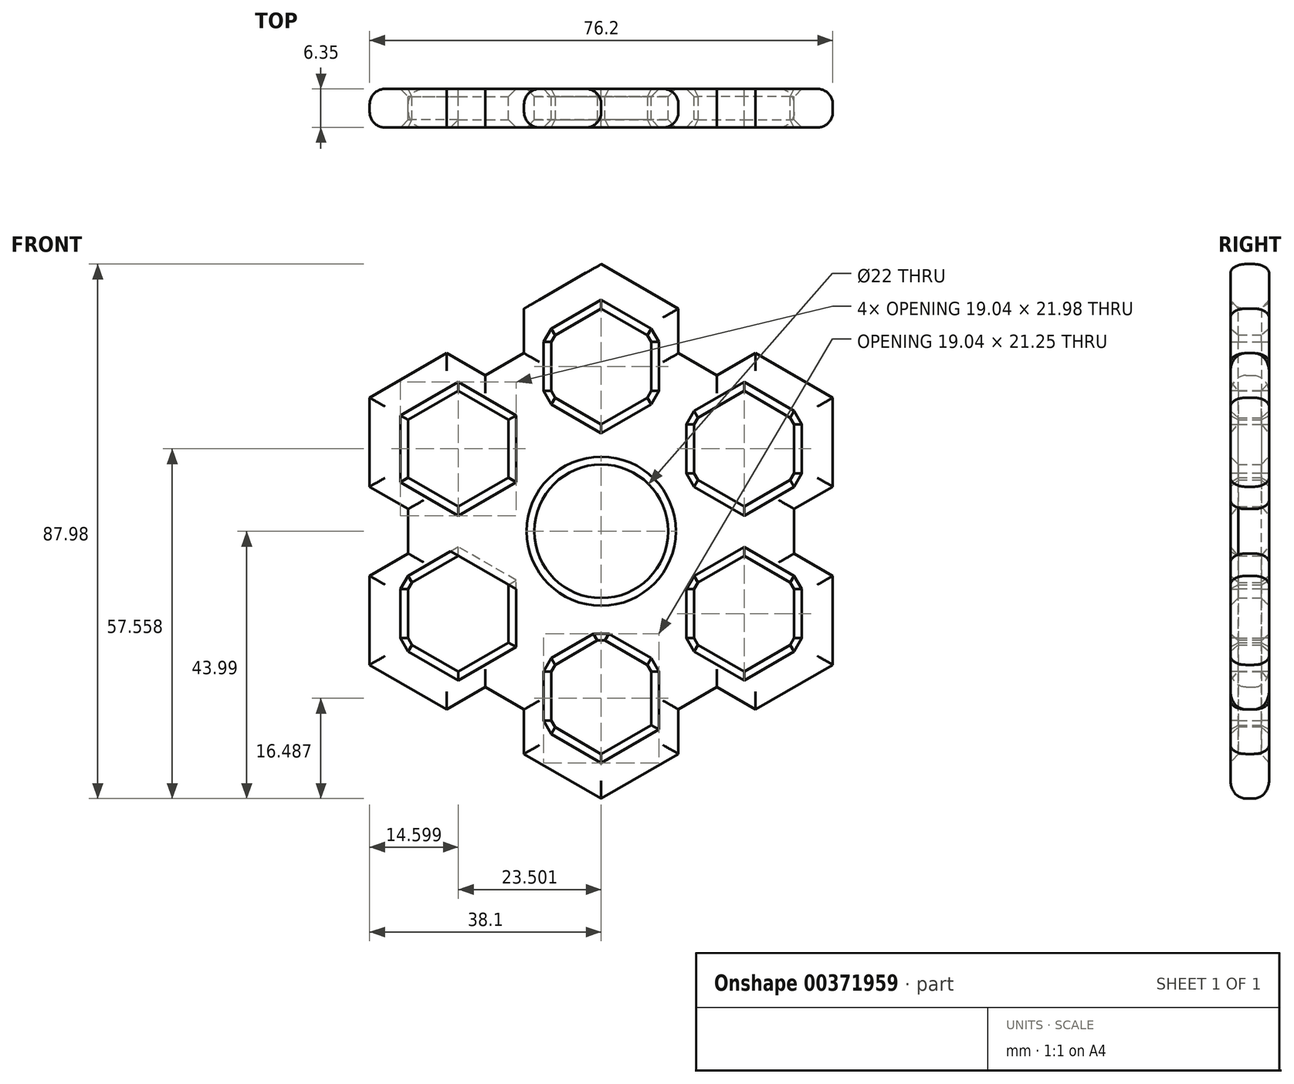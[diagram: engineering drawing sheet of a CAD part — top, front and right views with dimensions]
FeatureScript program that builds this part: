
annotation { "Feature Type Name" : "Feature", "Feature Type Description" : "" }
export const myFeature = defineFeature(function(context is Context, id is Id, definition is map)
    precondition{}
    {
        {
            var Q0;
            Q0=qCreatedBy(makeId("Front.planeOp"),FACE);
            var sketch = newSketch(context, id + "F0", { "sketchPlane" : qUnion([Q0])});
            skPoint(sketch, "E0", {"position": v(31.75, 0) * mm});
            skLineSegment(sketch, "E1.0", {"start": v(31.75, 18.33) * mm, "end": v(31.75, -18.33) * mm});
            skLineSegment(sketch, "E1.1", {"start": v(31.75, -18.33) * mm, "end": v(0, -36.66) * mm});
            skLineSegment(sketch, "E1.2", {"start": v(0, -36.66) * mm, "end": v(-31.75, -18.33) * mm});
            skLineSegment(sketch, "E1.3", {"start": v(-31.75, -18.33) * mm, "end": v(-31.75, 18.33) * mm});
            skLineSegment(sketch, "E1.4", {"start": v(-31.75, 18.33) * mm, "end": v(0, 36.66) * mm});
            skLineSegment(sketch, "E1.5", {"start": v(0, 36.66) * mm, "end": v(31.75, 18.33) * mm});
            skPoint(sketch, "E2.cCircle.center.orphan", {"position": v(0, 0) * mm});
            skCircle(sketch, "E3", {"center": v(0, 0) * mm, "radius": 11 * mm});
            skPoint(sketch, "E4", {"position": v(0, 27.14) * mm});
            skPoint(sketch, "E5", {"position": v(23.5, 13.57) * mm});
            skPoint(sketch, "E6", {"position": v(-23.5, 13.57) * mm});
            skPoint(sketch, "E7", {"position": v(-23.5, -13.57) * mm});
            skPoint(sketch, "E8", {"position": v(23.5, -13.57) * mm});
            skPoint(sketch, "E9", {"position": v(0, -27.14) * mm});
            skLineSegment(sketch, "E10.0", {"start": v(0, 36.66) * mm, "end": v(8.25, 31.9) * mm});
            skLineSegment(sketch, "E10.1", {"start": v(8.25, 31.9) * mm, "end": v(8.25, 22.37) * mm});
            skLineSegment(sketch, "E10.2", {"start": v(8.25, 22.37) * mm, "end": v(0, 17.61) * mm});
            skLineSegment(sketch, "E10.3", {"start": v(0, 17.61) * mm, "end": v(-8.25, 22.37) * mm});
            skLineSegment(sketch, "E10.4", {"start": v(-8.25, 22.37) * mm, "end": v(-8.25, 31.9) * mm});
            skLineSegment(sketch, "E10.5", {"start": v(-8.25, 31.9) * mm, "end": v(0, 36.66) * mm});
            skPoint(sketch, "E10.0.midPoint", {"position": v(4.12, 34.28) * mm});
            skLineSegment(sketch, "E11.0", {"start": v(8.25, -31.9) * mm, "end": v(0, -36.66) * mm});
            skLineSegment(sketch, "E11.1", {"start": v(0, -36.66) * mm, "end": v(-8.25, -31.9) * mm});
            skLineSegment(sketch, "E11.2", {"start": v(-8.25, -31.9) * mm, "end": v(-8.25, -22.37) * mm});
            skLineSegment(sketch, "E11.3", {"start": v(-8.25, -22.37) * mm, "end": v(0, -17.61) * mm});
            skLineSegment(sketch, "E11.4", {"start": v(0, -17.61) * mm, "end": v(8.25, -22.37) * mm});
            skLineSegment(sketch, "E11.5", {"start": v(8.25, -22.37) * mm, "end": v(8.25, -31.9) * mm});
            skPoint(sketch, "E11.0.midPoint", {"position": v(4.12, -34.28) * mm});
            skLineSegment(sketch, "E12.0", {"start": v(-31.75, 18.33) * mm, "end": v(-23.5, 23.1) * mm});
            skLineSegment(sketch, "E12.1", {"start": v(-23.5, 23.1) * mm, "end": v(-15.25, 18.33) * mm});
            skLineSegment(sketch, "E12.2", {"start": v(-15.25, 18.33) * mm, "end": v(-15.25, 8.8) * mm});
            skLineSegment(sketch, "E12.3", {"start": v(-15.25, 8.8) * mm, "end": v(-23.5, 4.04) * mm});
            skLineSegment(sketch, "E12.4", {"start": v(-23.5, 4.04) * mm, "end": v(-31.75, 8.8) * mm});
            skLineSegment(sketch, "E12.5", {"start": v(-31.75, 8.8) * mm, "end": v(-31.75, 18.33) * mm});
            skPoint(sketch, "E12.0.midPoint", {"position": v(-27.63, 20.71) * mm});
            skLineSegment(sketch, "E13.0", {"start": v(-31.75, -18.33) * mm, "end": v(-31.75, -8.8) * mm});
            skLineSegment(sketch, "E13.1", {"start": v(-31.75, -8.8) * mm, "end": v(-23.5, -4.04) * mm});
            skLineSegment(sketch, "E13.2", {"start": v(-23.5, -4.04) * mm, "end": v(-15.25, -8.8) * mm});
            skLineSegment(sketch, "E13.3", {"start": v(-15.25, -8.8) * mm, "end": v(-15.25, -18.33) * mm});
            skLineSegment(sketch, "E13.4", {"start": v(-15.25, -18.33) * mm, "end": v(-23.5, -23.1) * mm});
            skLineSegment(sketch, "E13.5", {"start": v(-23.5, -23.1) * mm, "end": v(-31.75, -18.33) * mm});
            skPoint(sketch, "E13.0.midPoint", {"position": v(-31.75, -13.57) * mm});
            skLineSegment(sketch, "E14.0", {"start": v(31.75, -18.33) * mm, "end": v(23.5, -23.1) * mm});
            skLineSegment(sketch, "E14.1", {"start": v(23.5, -23.1) * mm, "end": v(15.25, -18.33) * mm});
            skLineSegment(sketch, "E14.2", {"start": v(15.25, -18.33) * mm, "end": v(15.25, -8.8) * mm});
            skLineSegment(sketch, "E14.3", {"start": v(15.25, -8.8) * mm, "end": v(23.5, -4.04) * mm});
            skLineSegment(sketch, "E14.4", {"start": v(23.5, -4.04) * mm, "end": v(31.75, -8.8) * mm});
            skLineSegment(sketch, "E14.5", {"start": v(31.75, -8.8) * mm, "end": v(31.75, -18.33) * mm});
            skPoint(sketch, "E14.0.midPoint", {"position": v(27.63, -20.71) * mm});
            skLineSegment(sketch, "E15.0", {"start": v(31.75, 18.33) * mm, "end": v(31.75, 8.8) * mm});
            skLineSegment(sketch, "E15.1", {"start": v(31.75, 8.8) * mm, "end": v(23.5, 4.04) * mm});
            skLineSegment(sketch, "E15.2", {"start": v(23.5, 4.04) * mm, "end": v(15.25, 8.8) * mm});
            skLineSegment(sketch, "E15.3", {"start": v(15.25, 8.8) * mm, "end": v(15.25, 18.33) * mm});
            skLineSegment(sketch, "E15.4", {"start": v(15.25, 18.33) * mm, "end": v(23.5, 23.1) * mm});
            skLineSegment(sketch, "E15.5", {"start": v(23.5, 23.1) * mm, "end": v(31.75, 18.33) * mm});
            skPoint(sketch, "E15.0.midPoint", {"position": v(31.75, 13.57) * mm});
            skArc(sketch, "E16.trimOffspring", {"start": v(-4.12, 34.28) * mm, "mid": v(-7.14, 31.26) * mm, "end": v(-8.25, 27.14) * mm, "construction": true});
            skPoint(sketch, "E17", {"position": v(38.1, 0) * mm});
            skLineSegment(sketch, "E18.0", {"start": v(38.1, 22) * mm, "end": v(38.1, -22) * mm});
            skLineSegment(sketch, "E18.1", {"start": v(38.1, -22) * mm, "end": v(0, -44) * mm});
            skLineSegment(sketch, "E18.2", {"start": v(0, -44) * mm, "end": v(-38.1, -22) * mm});
            skLineSegment(sketch, "E18.3", {"start": v(-38.1, -22) * mm, "end": v(-38.1, 22) * mm});
            skLineSegment(sketch, "E18.4", {"start": v(-38.1, 22) * mm, "end": v(-25.4, 29.33) * mm});
            skLineSegment(sketch, "E18.5", {"start": v(0, 44) * mm, "end": v(38.1, 22) * mm});
            skLineSegment(sketch, "E19.0", {"start": v(-12.7, 29.33) * mm, "end": v(-19.05, 25.66) * mm});
            skLineSegment(sketch, "E19.1", {"start": v(-19.05, 25.66) * mm, "end": v(-25.4, 29.33) * mm});
            skLineSegment(sketch, "E19.5", {"start": v(-12.7, 36.66) * mm, "end": v(-12.7, 29.33) * mm});
            skPoint(sketch, "E19.0.midPoint", {"position": v(-15.88, 27.5) * mm});
            skCircle(sketch, "E20.cCircle", {"center": v(19.05, 33) * mm, "radius": 6.35 * mm, "construction": true});
            skLineSegment(sketch, "E20.0", {"start": v(19.05, 25.66) * mm, "end": v(12.7, 29.33) * mm});
            skLineSegment(sketch, "E20.1", {"start": v(12.7, 29.33) * mm, "end": v(12.7, 36.66) * mm});
            skLineSegment(sketch, "E20.2", {"start": v(12.7, 36.66) * mm, "end": v(19.05, 40.33) * mm});
            skLineSegment(sketch, "E20.3", {"start": v(19.05, 40.33) * mm, "end": v(25.4, 36.66) * mm});
            skLineSegment(sketch, "E20.4", {"start": v(25.4, 36.66) * mm, "end": v(25.4, 29.33) * mm});
            skLineSegment(sketch, "E20.5", {"start": v(25.4, 29.33) * mm, "end": v(19.05, 25.66) * mm});
            skPoint(sketch, "E20.0.midPoint", {"position": v(15.87, 27.5) * mm});
            skCircle(sketch, "E21.cCircle", {"center": v(38.1, 0) * mm, "radius": 6.35 * mm, "construction": true});
            skLineSegment(sketch, "E21.0", {"start": v(31.75, -3.67) * mm, "end": v(31.75, 3.67) * mm});
            skLineSegment(sketch, "E21.1", {"start": v(31.75, 3.67) * mm, "end": v(38.1, 7.33) * mm});
            skLineSegment(sketch, "E21.2", {"start": v(38.1, 7.33) * mm, "end": v(44.45, 3.67) * mm});
            skLineSegment(sketch, "E21.3", {"start": v(44.45, 3.67) * mm, "end": v(44.45, -3.67) * mm});
            skLineSegment(sketch, "E21.4", {"start": v(44.45, -3.67) * mm, "end": v(38.1, -7.33) * mm});
            skLineSegment(sketch, "E21.5", {"start": v(38.1, -7.33) * mm, "end": v(31.75, -3.67) * mm});
            skCircle(sketch, "E22.cCircle", {"center": v(19.05, -33) * mm, "radius": 6.35 * mm, "construction": true});
            skLineSegment(sketch, "E22.0", {"start": v(12.7, -29.33) * mm, "end": v(19.05, -25.66) * mm});
            skLineSegment(sketch, "E22.1", {"start": v(19.05, -25.66) * mm, "end": v(25.4, -29.33) * mm});
            skLineSegment(sketch, "E22.2", {"start": v(25.4, -29.33) * mm, "end": v(25.4, -36.66) * mm});
            skLineSegment(sketch, "E22.3", {"start": v(25.4, -36.66) * mm, "end": v(19.05, -40.33) * mm});
            skLineSegment(sketch, "E22.4", {"start": v(19.05, -40.33) * mm, "end": v(12.7, -36.66) * mm});
            skLineSegment(sketch, "E22.5", {"start": v(12.7, -36.66) * mm, "end": v(12.7, -29.33) * mm});
            skPoint(sketch, "E22.0.midPoint", {"position": v(15.87, -27.5) * mm});
            skCircle(sketch, "E23.cCircle", {"center": v(-19.05, -33) * mm, "radius": 6.35 * mm, "construction": true});
            skLineSegment(sketch, "E23.0", {"start": v(-19.05, -25.66) * mm, "end": v(-12.7, -29.33) * mm});
            skLineSegment(sketch, "E23.1", {"start": v(-12.7, -29.33) * mm, "end": v(-12.7, -36.66) * mm});
            skLineSegment(sketch, "E23.2", {"start": v(-12.7, -36.66) * mm, "end": v(-19.05, -40.33) * mm});
            skLineSegment(sketch, "E23.3", {"start": v(-19.05, -40.33) * mm, "end": v(-25.4, -36.66) * mm});
            skLineSegment(sketch, "E23.4", {"start": v(-25.4, -36.66) * mm, "end": v(-25.4, -29.33) * mm});
            skLineSegment(sketch, "E23.5", {"start": v(-25.4, -29.33) * mm, "end": v(-19.05, -25.66) * mm});
            skPoint(sketch, "E23.0.midPoint", {"position": v(-15.88, -27.5) * mm});
            skCircle(sketch, "E24.cCircle", {"center": v(-38.1, 0) * mm, "radius": 6.35 * mm, "construction": true});
            skLineSegment(sketch, "E24.0", {"start": v(-31.75, 3.67) * mm, "end": v(-31.75, -3.67) * mm});
            skLineSegment(sketch, "E24.1", {"start": v(-31.75, -3.67) * mm, "end": v(-38.1, -7.33) * mm});
            skLineSegment(sketch, "E24.2", {"start": v(-38.1, -7.33) * mm, "end": v(-44.45, -3.67) * mm});
            skLineSegment(sketch, "E24.3", {"start": v(-44.45, -3.67) * mm, "end": v(-44.45, 3.67) * mm});
            skLineSegment(sketch, "E24.4", {"start": v(-44.45, 3.67) * mm, "end": v(-38.1, 7.33) * mm});
            skLineSegment(sketch, "E24.5", {"start": v(-38.1, 7.33) * mm, "end": v(-31.75, 3.67) * mm});
            skPoint(sketch, "E24.0.midPoint", {"position": v(-31.75, 0) * mm});
            skLineSegment(sketch, "E25.trimOffspring", {"start": v(-12.7, 36.66) * mm, "end": v(0, 44) * mm});
            skSolve(sketch);
        }
        {
            var Q0;
            Q0=makeQuery(id+"F0.imprint","IMPRINT",FACE,{"disambiguationData":[TD([[makeQuery(id+"F0.imprint","IMPRINT",EDGE,{"derivedFrom":sQuery(id+"F0.wireOp",EDGE,"E3")}),-1.0]])]});
            var Q1;
            {var subQ2=sQuery(id+"F0.wireOp",EDGE,"E20.5");Q1=makeQuery(id+"F0.imprint","IMPRINT",FACE,{"disambiguationData":[TD([[makeQuery(id+"F0.imprint","IMPRINT",EDGE,{"derivedFrom":subQ2}),1.0]])]});}
            var Q2;
            {var subQ6=sQuery(id+"F0.wireOp",EDGE,"E21.5");Q2=makeQuery(id+"F0.imprint","IMPRINT",FACE,{"disambiguationData":[TD([[makeQuery(id+"F0.imprint","IMPRINT",EDGE,{"derivedFrom":subQ6}),1.0]])]});}
            var Q3;
            {var subQ5=sQuery(id+"F0.wireOp",EDGE,"E22.5");Q3=makeQuery(id+"F0.imprint","IMPRINT",FACE,{"disambiguationData":[TD([[makeQuery(id+"F0.imprint","IMPRINT",EDGE,{"derivedFrom":subQ5}),1.0]])]});}
            var Q4;
            {var subQ3=sQuery(id+"F0.wireOp",EDGE,"E23.5");Q4=makeQuery(id+"F0.imprint","IMPRINT",FACE,{"disambiguationData":[TD([[makeQuery(id+"F0.imprint","IMPRINT",EDGE,{"derivedFrom":subQ3}),1.0]])]});}
            var Q5;
            {var subQ0=sQuery(id+"F0.wireOp",EDGE,"E19.1");Q5=makeQuery(id+"F0.imprint","IMPRINT",FACE,{"disambiguationData":[TD([[makeQuery(id+"F0.imprint","IMPRINT",EDGE,{"derivedFrom":subQ0}),1.0]])]});}
            var Q6;
            {var subQ6=sQuery(id+"F0.wireOp",EDGE,"E19.5");Q6=makeQuery(id+"F0.imprint","IMPRINT",FACE,{"disambiguationData":[TD([[makeQuery(id+"F0.imprint","IMPRINT",EDGE,{"derivedFrom":subQ6}),1.0]])]});}
            extrude(context, id + "F1", {"entities" : qUnion([Q0, Q1, Q2, Q3, Q4, Q5, Q6]), "depth" : 6.35 * mm, "offsetDistance" : 25.4 * mm});
        }
        {
            var Q0;
            Q0=makeQuery(id+"F1.opExtrude","CAP_EDGE",EDGE,{"disambiguationData":[OSD([sQuery(id+"F0.wireOp",EDGE,"E19.1")])],"isStart":false});
            var Q1;
            {var subQ0=sQuery(id+"F0.wireOp",EDGE,"E1.4");Q1=makeQuery(id+"F1.opExtrude","CAP_EDGE",EDGE,{"disambiguationData":[OSD([subQ0]),TDD([makeQuery(id+"F0.imprint","IMPRINT",EDGE,{"disambiguationData":[TD([[makeQuery(id+"F0.imprint","INTERSECT",VERTEX,{"derivedFrom":[subQ0,sQuery(id+"F0.wireOp",EDGE,"E19.1")]}),-1.0]])],"derivedFrom":subQ0})])],"isStart":false});}
            var Q2;
            Q2=makeQuery(id+"F1.opExtrude","CAP_EDGE",EDGE,{"disambiguationData":[OSD([sQuery(id+"F0.wireOp",EDGE,"E19.5")])],"isStart":false});
            var Q3;
            {var subQ0=sQuery(id+"F0.wireOp",EDGE,"E18.4");Q3=makeQuery(id+"F1.opExtrude","CAP_EDGE",EDGE,{"disambiguationData":[OSD([subQ0]),TDD([makeQuery(id+"F0.imprint","IMPRINT",EDGE,{"disambiguationData":[TD([[makeQuery(id+"F0.imprint","INTERSECT",VERTEX,{"derivedFrom":[subQ0,sQuery(id+"F0.wireOp",EDGE,"E18.5")]}),1.0]])],"derivedFrom":subQ0})])],"isStart":false});}
            var Q4;
            {var subQ0=sQuery(id+"F0.wireOp",EDGE,"E18.5");Q4=makeQuery(id+"F1.opExtrude","CAP_EDGE",EDGE,{"disambiguationData":[OSD([subQ0]),TDD([makeQuery(id+"F0.imprint","IMPRINT",EDGE,{"disambiguationData":[TD([[makeQuery(id+"F0.imprint","INTERSECT",VERTEX,{"derivedFrom":[sQuery(id+"F0.wireOp",EDGE,"E18.4"),subQ0]}),-1.0]])],"derivedFrom":subQ0})])],"isStart":false});}
            var Q5;
            Q5=makeQuery(id+"F1.opExtrude","CAP_EDGE",EDGE,{"disambiguationData":[OSD([sQuery(id+"F0.wireOp",EDGE,"E20.1")])],"isStart":false});
            var Q6;
            {var subQ0=sQuery(id+"F0.wireOp",EDGE,"E1.5");Q6=makeQuery(id+"F1.opExtrude","CAP_EDGE",EDGE,{"disambiguationData":[OSD([subQ0]),TDD([makeQuery(id+"F0.imprint","IMPRINT",EDGE,{"disambiguationData":[TD([[makeQuery(id+"F0.imprint","INTERSECT",VERTEX,{"derivedFrom":[subQ0,sQuery(id+"F0.wireOp",EDGE,"E20.1")]}),-1.0]])],"derivedFrom":subQ0})])],"isStart":false});}
            var Q7;
            Q7=makeQuery(id+"F1.opExtrude","CAP_EDGE",EDGE,{"disambiguationData":[OSD([sQuery(id+"F0.wireOp",EDGE,"E20.5")])],"isStart":false});
            var Q8;
            {var subQ0=sQuery(id+"F0.wireOp",EDGE,"E18.5");Q8=makeQuery(id+"F1.opExtrude","CAP_EDGE",EDGE,{"disambiguationData":[OSD([subQ0]),TDD([makeQuery(id+"F0.imprint","IMPRINT",EDGE,{"disambiguationData":[TD([[makeQuery(id+"F0.imprint","INTERSECT",VERTEX,{"derivedFrom":[sQuery(id+"F0.wireOp",EDGE,"E18.0"),subQ0]}),1.0]])],"derivedFrom":subQ0})])],"isStart":false});}
            var Q9;
            {var subQ0=sQuery(id+"F0.wireOp",EDGE,"E18.0");Q9=makeQuery(id+"F1.opExtrude","CAP_EDGE",EDGE,{"disambiguationData":[OSD([subQ0]),TDD([makeQuery(id+"F0.imprint","IMPRINT",EDGE,{"disambiguationData":[TD([[makeQuery(id+"F0.imprint","INTERSECT",VERTEX,{"derivedFrom":[subQ0,sQuery(id+"F0.wireOp",EDGE,"E18.5")]}),-1.0]])],"derivedFrom":subQ0})])],"isStart":false});}
            var Q10;
            Q10=makeQuery(id+"F1.opExtrude","CAP_EDGE",EDGE,{"disambiguationData":[OSD([sQuery(id+"F0.wireOp",EDGE,"E21.1")])],"isStart":false});
            var Q11;
            {var subQ0=sQuery(id+"F0.wireOp",EDGE,"E1.0");Q11=makeQuery(id+"F1.opExtrude","CAP_EDGE",EDGE,{"disambiguationData":[OSD([subQ0]),TDD([makeQuery(id+"F0.imprint","IMPRINT",EDGE,{"disambiguationData":[TD([[makeQuery(id+"F0.imprint","INTERSECT",VERTEX,{"derivedFrom":[subQ0,sQuery(id+"F0.wireOp",EDGE,"E21.1")]}),-1.0]])],"derivedFrom":subQ0})])],"isStart":false});}
            var Q12;
            Q12=makeQuery(id+"F1.opExtrude","CAP_EDGE",EDGE,{"disambiguationData":[OSD([sQuery(id+"F0.wireOp",EDGE,"E21.5")])],"isStart":false});
            var Q13;
            {var subQ0=sQuery(id+"F0.wireOp",EDGE,"E18.0");Q13=makeQuery(id+"F1.opExtrude","CAP_EDGE",EDGE,{"disambiguationData":[OSD([subQ0]),TDD([makeQuery(id+"F0.imprint","IMPRINT",EDGE,{"disambiguationData":[TD([[makeQuery(id+"F0.imprint","INTERSECT",VERTEX,{"derivedFrom":[subQ0,sQuery(id+"F0.wireOp",EDGE,"E18.1")]}),1.0]])],"derivedFrom":subQ0})])],"isStart":false});}
            var Q14;
            {var subQ0=sQuery(id+"F0.wireOp",EDGE,"E18.1");Q14=makeQuery(id+"F1.opExtrude","CAP_EDGE",EDGE,{"disambiguationData":[OSD([subQ0]),TDD([makeQuery(id+"F0.imprint","IMPRINT",EDGE,{"disambiguationData":[TD([[makeQuery(id+"F0.imprint","INTERSECT",VERTEX,{"derivedFrom":[sQuery(id+"F0.wireOp",EDGE,"E18.0"),subQ0]}),-1.0]])],"derivedFrom":subQ0})])],"isStart":false});}
            var Q15;
            Q15=makeQuery(id+"F1.opExtrude","CAP_EDGE",EDGE,{"disambiguationData":[OSD([sQuery(id+"F0.wireOp",EDGE,"E22.1")])],"isStart":false});
            var Q16;
            {var subQ0=sQuery(id+"F0.wireOp",EDGE,"E1.1");Q16=makeQuery(id+"F1.opExtrude","CAP_EDGE",EDGE,{"disambiguationData":[OSD([subQ0]),TDD([makeQuery(id+"F0.imprint","IMPRINT",EDGE,{"disambiguationData":[TD([[makeQuery(id+"F0.imprint","INTERSECT",VERTEX,{"derivedFrom":[subQ0,sQuery(id+"F0.wireOp",EDGE,"E22.1")]}),-1.0]])],"derivedFrom":subQ0})])],"isStart":false});}
            var Q17;
            Q17=makeQuery(id+"F1.opExtrude","CAP_EDGE",EDGE,{"disambiguationData":[OSD([sQuery(id+"F0.wireOp",EDGE,"E22.5")])],"isStart":false});
            var Q18;
            {var subQ0=sQuery(id+"F0.wireOp",EDGE,"E18.1");Q18=makeQuery(id+"F1.opExtrude","CAP_EDGE",EDGE,{"disambiguationData":[OSD([subQ0]),TDD([makeQuery(id+"F0.imprint","IMPRINT",EDGE,{"disambiguationData":[TD([[makeQuery(id+"F0.imprint","INTERSECT",VERTEX,{"derivedFrom":[subQ0,sQuery(id+"F0.wireOp",EDGE,"E18.2")]}),1.0]])],"derivedFrom":subQ0})])],"isStart":false});}
            var Q19;
            {var subQ0=sQuery(id+"F0.wireOp",EDGE,"E18.2");Q19=makeQuery(id+"F1.opExtrude","CAP_EDGE",EDGE,{"disambiguationData":[OSD([subQ0]),TDD([makeQuery(id+"F0.imprint","IMPRINT",EDGE,{"disambiguationData":[TD([[makeQuery(id+"F0.imprint","INTERSECT",VERTEX,{"derivedFrom":[sQuery(id+"F0.wireOp",EDGE,"E18.1"),subQ0]}),-1.0]])],"derivedFrom":subQ0})])],"isStart":false});}
            var Q20;
            Q20=makeQuery(id+"F1.opExtrude","CAP_EDGE",EDGE,{"disambiguationData":[OSD([sQuery(id+"F0.wireOp",EDGE,"E23.1")])],"isStart":false});
            var Q21;
            {var subQ0=sQuery(id+"F0.wireOp",EDGE,"E1.2");Q21=makeQuery(id+"F1.opExtrude","CAP_EDGE",EDGE,{"disambiguationData":[OSD([subQ0]),TDD([makeQuery(id+"F0.imprint","IMPRINT",EDGE,{"disambiguationData":[TD([[makeQuery(id+"F0.imprint","INTERSECT",VERTEX,{"derivedFrom":[subQ0,sQuery(id+"F0.wireOp",EDGE,"E23.1")]}),-1.0]])],"derivedFrom":subQ0})])],"isStart":false});}
            var Q22;
            Q22=makeQuery(id+"F1.opExtrude","CAP_EDGE",EDGE,{"disambiguationData":[OSD([sQuery(id+"F0.wireOp",EDGE,"E23.5")])],"isStart":false});
            var Q23;
            {var subQ0=sQuery(id+"F0.wireOp",EDGE,"E18.2");Q23=makeQuery(id+"F1.opExtrude","CAP_EDGE",EDGE,{"disambiguationData":[OSD([subQ0]),TDD([makeQuery(id+"F0.imprint","IMPRINT",EDGE,{"disambiguationData":[TD([[makeQuery(id+"F0.imprint","INTERSECT",VERTEX,{"derivedFrom":[subQ0,sQuery(id+"F0.wireOp",EDGE,"E18.3")]}),1.0]])],"derivedFrom":subQ0})])],"isStart":false});}
            var Q24;
            {var subQ0=sQuery(id+"F0.wireOp",EDGE,"E18.3");Q24=makeQuery(id+"F1.opExtrude","CAP_EDGE",EDGE,{"disambiguationData":[OSD([subQ0]),TDD([makeQuery(id+"F0.imprint","IMPRINT",EDGE,{"disambiguationData":[TD([[makeQuery(id+"F0.imprint","INTERSECT",VERTEX,{"derivedFrom":[sQuery(id+"F0.wireOp",EDGE,"E18.2"),subQ0]}),-1.0]])],"derivedFrom":subQ0})])],"isStart":false});}
            var Q25;
            Q25=makeQuery(id+"F1.opExtrude","CAP_EDGE",EDGE,{"disambiguationData":[OSD([sQuery(id+"F0.wireOp",EDGE,"E24.1")])],"isStart":false});
            var Q26;
            {var subQ0=sQuery(id+"F0.wireOp",EDGE,"E18.4");Q26=makeQuery(id+"F1.opExtrude","CAP_EDGE",EDGE,{"disambiguationData":[OSD([subQ0]),TDD([makeQuery(id+"F0.imprint","IMPRINT",EDGE,{"disambiguationData":[TD([[makeQuery(id+"F0.imprint","INTERSECT",VERTEX,{"derivedFrom":[sQuery(id+"F0.wireOp",EDGE,"E18.3"),subQ0]}),-1.0]])],"derivedFrom":subQ0})])],"isStart":false});}
            var Q27;
            {var subQ0=sQuery(id+"F0.wireOp",EDGE,"E1.3");Q27=makeQuery(id+"F1.opExtrude","CAP_EDGE",EDGE,{"disambiguationData":[OSD([subQ0]),TDD([makeQuery(id+"F0.imprint","IMPRINT",EDGE,{"disambiguationData":[TD([[makeQuery(id+"F0.imprint","INTERSECT",VERTEX,{"derivedFrom":[subQ0,sQuery(id+"F0.wireOp",EDGE,"E24.1")]}),-1.0]])],"derivedFrom":subQ0})])],"isStart":false});}
            var Q28;
            Q28=makeQuery(id+"F1.opExtrude","CAP_EDGE",EDGE,{"disambiguationData":[OSD([sQuery(id+"F0.wireOp",EDGE,"E24.5")])],"isStart":false});
            var Q29;
            {var subQ0=sQuery(id+"F0.wireOp",EDGE,"E18.3");Q29=makeQuery(id+"F1.opExtrude","CAP_EDGE",EDGE,{"disambiguationData":[OSD([subQ0]),TDD([makeQuery(id+"F0.imprint","IMPRINT",EDGE,{"disambiguationData":[TD([[makeQuery(id+"F0.imprint","INTERSECT",VERTEX,{"derivedFrom":[subQ0,sQuery(id+"F0.wireOp",EDGE,"E18.4")]}),1.0]])],"derivedFrom":subQ0})])],"isStart":false});}
            var Q30;
            {var subQ0=sQuery(id+"F0.wireOp",EDGE,"E18.4");Q30=makeQuery(id+"F1.opExtrude","CAP_EDGE",EDGE,{"disambiguationData":[OSD([subQ0]),TDD([makeQuery(id+"F0.imprint","IMPRINT",EDGE,{"disambiguationData":[TD([[makeQuery(id+"F0.imprint","INTERSECT",VERTEX,{"derivedFrom":[subQ0,sQuery(id+"F0.wireOp",EDGE,"E18.5")]}),1.0]])],"derivedFrom":subQ0})])],"isStart":true});}
            var Q31;
            {var subQ0=sQuery(id+"F0.wireOp",EDGE,"E18.5");Q31=makeQuery(id+"F1.opExtrude","CAP_EDGE",EDGE,{"disambiguationData":[OSD([subQ0]),TDD([makeQuery(id+"F0.imprint","IMPRINT",EDGE,{"disambiguationData":[TD([[makeQuery(id+"F0.imprint","INTERSECT",VERTEX,{"derivedFrom":[sQuery(id+"F0.wireOp",EDGE,"E18.4"),subQ0]}),-1.0]])],"derivedFrom":subQ0})])],"isStart":true});}
            var Q32;
            Q32=makeQuery(id+"F1.opExtrude","CAP_EDGE",EDGE,{"disambiguationData":[OSD([sQuery(id+"F0.wireOp",EDGE,"E20.1")])],"isStart":true});
            var Q33;
            {var subQ0=sQuery(id+"F0.wireOp",EDGE,"E1.5");Q33=makeQuery(id+"F1.opExtrude","CAP_EDGE",EDGE,{"disambiguationData":[OSD([subQ0]),TDD([makeQuery(id+"F0.imprint","IMPRINT",EDGE,{"disambiguationData":[TD([[makeQuery(id+"F0.imprint","INTERSECT",VERTEX,{"derivedFrom":[subQ0,sQuery(id+"F0.wireOp",EDGE,"E20.1")]}),-1.0]])],"derivedFrom":subQ0})])],"isStart":true});}
            var Q34;
            Q34=makeQuery(id+"F1.opExtrude","CAP_EDGE",EDGE,{"disambiguationData":[OSD([sQuery(id+"F0.wireOp",EDGE,"E20.5")])],"isStart":true});
            var Q35;
            {var subQ0=sQuery(id+"F0.wireOp",EDGE,"E18.5");Q35=makeQuery(id+"F1.opExtrude","CAP_EDGE",EDGE,{"disambiguationData":[OSD([subQ0]),TDD([makeQuery(id+"F0.imprint","IMPRINT",EDGE,{"disambiguationData":[TD([[makeQuery(id+"F0.imprint","INTERSECT",VERTEX,{"derivedFrom":[sQuery(id+"F0.wireOp",EDGE,"E18.0"),subQ0]}),1.0]])],"derivedFrom":subQ0})])],"isStart":true});}
            var Q36;
            {var subQ0=sQuery(id+"F0.wireOp",EDGE,"E18.0");Q36=makeQuery(id+"F1.opExtrude","CAP_EDGE",EDGE,{"disambiguationData":[OSD([subQ0]),TDD([makeQuery(id+"F0.imprint","IMPRINT",EDGE,{"disambiguationData":[TD([[makeQuery(id+"F0.imprint","INTERSECT",VERTEX,{"derivedFrom":[subQ0,sQuery(id+"F0.wireOp",EDGE,"E18.5")]}),-1.0]])],"derivedFrom":subQ0})])],"isStart":true});}
            var Q37;
            Q37=makeQuery(id+"F1.opExtrude","CAP_EDGE",EDGE,{"disambiguationData":[OSD([sQuery(id+"F0.wireOp",EDGE,"E21.1")])],"isStart":true});
            var Q38;
            {var subQ0=sQuery(id+"F0.wireOp",EDGE,"E1.0");Q38=makeQuery(id+"F1.opExtrude","CAP_EDGE",EDGE,{"disambiguationData":[OSD([subQ0]),TDD([makeQuery(id+"F0.imprint","IMPRINT",EDGE,{"disambiguationData":[TD([[makeQuery(id+"F0.imprint","INTERSECT",VERTEX,{"derivedFrom":[subQ0,sQuery(id+"F0.wireOp",EDGE,"E21.1")]}),-1.0]])],"derivedFrom":subQ0})])],"isStart":true});}
            var Q39;
            Q39=makeQuery(id+"F1.opExtrude","CAP_EDGE",EDGE,{"disambiguationData":[OSD([sQuery(id+"F0.wireOp",EDGE,"E21.5")])],"isStart":true});
            var Q40;
            {var subQ0=sQuery(id+"F0.wireOp",EDGE,"E18.0");Q40=makeQuery(id+"F1.opExtrude","CAP_EDGE",EDGE,{"disambiguationData":[OSD([subQ0]),TDD([makeQuery(id+"F0.imprint","IMPRINT",EDGE,{"disambiguationData":[TD([[makeQuery(id+"F0.imprint","INTERSECT",VERTEX,{"derivedFrom":[subQ0,sQuery(id+"F0.wireOp",EDGE,"E18.1")]}),1.0]])],"derivedFrom":subQ0})])],"isStart":true});}
            var Q41;
            {var subQ0=sQuery(id+"F0.wireOp",EDGE,"E18.1");Q41=makeQuery(id+"F1.opExtrude","CAP_EDGE",EDGE,{"disambiguationData":[OSD([subQ0]),TDD([makeQuery(id+"F0.imprint","IMPRINT",EDGE,{"disambiguationData":[TD([[makeQuery(id+"F0.imprint","INTERSECT",VERTEX,{"derivedFrom":[sQuery(id+"F0.wireOp",EDGE,"E18.0"),subQ0]}),-1.0]])],"derivedFrom":subQ0})])],"isStart":true});}
            var Q42;
            Q42=makeQuery(id+"F1.opExtrude","CAP_EDGE",EDGE,{"disambiguationData":[OSD([sQuery(id+"F0.wireOp",EDGE,"E22.1")])],"isStart":true});
            var Q43;
            {var subQ0=sQuery(id+"F0.wireOp",EDGE,"E1.1");Q43=makeQuery(id+"F1.opExtrude","CAP_EDGE",EDGE,{"disambiguationData":[OSD([subQ0]),TDD([makeQuery(id+"F0.imprint","IMPRINT",EDGE,{"disambiguationData":[TD([[makeQuery(id+"F0.imprint","INTERSECT",VERTEX,{"derivedFrom":[subQ0,sQuery(id+"F0.wireOp",EDGE,"E22.1")]}),-1.0]])],"derivedFrom":subQ0})])],"isStart":true});}
            var Q44;
            Q44=makeQuery(id+"F1.opExtrude","CAP_EDGE",EDGE,{"disambiguationData":[OSD([sQuery(id+"F0.wireOp",EDGE,"E22.5")])],"isStart":true});
            var Q45;
            {var subQ0=sQuery(id+"F0.wireOp",EDGE,"E18.1");Q45=makeQuery(id+"F1.opExtrude","CAP_EDGE",EDGE,{"disambiguationData":[OSD([subQ0]),TDD([makeQuery(id+"F0.imprint","IMPRINT",EDGE,{"disambiguationData":[TD([[makeQuery(id+"F0.imprint","INTERSECT",VERTEX,{"derivedFrom":[subQ0,sQuery(id+"F0.wireOp",EDGE,"E18.2")]}),1.0]])],"derivedFrom":subQ0})])],"isStart":true});}
            var Q46;
            {var subQ0=sQuery(id+"F0.wireOp",EDGE,"E18.2");Q46=makeQuery(id+"F1.opExtrude","CAP_EDGE",EDGE,{"disambiguationData":[OSD([subQ0]),TDD([makeQuery(id+"F0.imprint","IMPRINT",EDGE,{"disambiguationData":[TD([[makeQuery(id+"F0.imprint","INTERSECT",VERTEX,{"derivedFrom":[sQuery(id+"F0.wireOp",EDGE,"E18.1"),subQ0]}),-1.0]])],"derivedFrom":subQ0})])],"isStart":true});}
            var Q47;
            Q47=makeQuery(id+"F1.opExtrude","CAP_EDGE",EDGE,{"disambiguationData":[OSD([sQuery(id+"F0.wireOp",EDGE,"E23.1")])],"isStart":true});
            var Q48;
            {var subQ0=sQuery(id+"F0.wireOp",EDGE,"E1.2");Q48=makeQuery(id+"F1.opExtrude","CAP_EDGE",EDGE,{"disambiguationData":[OSD([subQ0]),TDD([makeQuery(id+"F0.imprint","IMPRINT",EDGE,{"disambiguationData":[TD([[makeQuery(id+"F0.imprint","INTERSECT",VERTEX,{"derivedFrom":[subQ0,sQuery(id+"F0.wireOp",EDGE,"E23.1")]}),-1.0]])],"derivedFrom":subQ0})])],"isStart":true});}
            var Q49;
            Q49=makeQuery(id+"F1.opExtrude","CAP_EDGE",EDGE,{"disambiguationData":[OSD([sQuery(id+"F0.wireOp",EDGE,"E23.5")])],"isStart":true});
            var Q50;
            {var subQ0=sQuery(id+"F0.wireOp",EDGE,"E18.2");Q50=makeQuery(id+"F1.opExtrude","CAP_EDGE",EDGE,{"disambiguationData":[OSD([subQ0]),TDD([makeQuery(id+"F0.imprint","IMPRINT",EDGE,{"disambiguationData":[TD([[makeQuery(id+"F0.imprint","INTERSECT",VERTEX,{"derivedFrom":[subQ0,sQuery(id+"F0.wireOp",EDGE,"E18.3")]}),1.0]])],"derivedFrom":subQ0})])],"isStart":true});}
            var Q51;
            {var subQ0=sQuery(id+"F0.wireOp",EDGE,"E18.3");Q51=makeQuery(id+"F1.opExtrude","CAP_EDGE",EDGE,{"disambiguationData":[OSD([subQ0]),TDD([makeQuery(id+"F0.imprint","IMPRINT",EDGE,{"disambiguationData":[TD([[makeQuery(id+"F0.imprint","INTERSECT",VERTEX,{"derivedFrom":[sQuery(id+"F0.wireOp",EDGE,"E18.2"),subQ0]}),-1.0]])],"derivedFrom":subQ0})])],"isStart":true});}
            var Q52;
            Q52=makeQuery(id+"F1.opExtrude","CAP_EDGE",EDGE,{"disambiguationData":[OSD([sQuery(id+"F0.wireOp",EDGE,"E24.1")])],"isStart":true});
            var Q53;
            {var subQ0=sQuery(id+"F0.wireOp",EDGE,"E1.3");Q53=makeQuery(id+"F1.opExtrude","CAP_EDGE",EDGE,{"disambiguationData":[OSD([subQ0]),TDD([makeQuery(id+"F0.imprint","IMPRINT",EDGE,{"disambiguationData":[TD([[makeQuery(id+"F0.imprint","INTERSECT",VERTEX,{"derivedFrom":[subQ0,sQuery(id+"F0.wireOp",EDGE,"E24.1")]}),-1.0]])],"derivedFrom":subQ0})])],"isStart":true});}
            var Q54;
            Q54=makeQuery(id+"F1.opExtrude","CAP_EDGE",EDGE,{"disambiguationData":[OSD([sQuery(id+"F0.wireOp",EDGE,"E24.5")])],"isStart":true});
            var Q55;
            {var subQ0=sQuery(id+"F0.wireOp",EDGE,"E18.3");Q55=makeQuery(id+"F1.opExtrude","CAP_EDGE",EDGE,{"disambiguationData":[OSD([subQ0]),TDD([makeQuery(id+"F0.imprint","IMPRINT",EDGE,{"disambiguationData":[TD([[makeQuery(id+"F0.imprint","INTERSECT",VERTEX,{"derivedFrom":[subQ0,sQuery(id+"F0.wireOp",EDGE,"E18.4")]}),1.0]])],"derivedFrom":subQ0})])],"isStart":true});}
            var Q56;
            {var subQ0=sQuery(id+"F0.wireOp",EDGE,"E18.4");Q56=makeQuery(id+"F1.opExtrude","CAP_EDGE",EDGE,{"disambiguationData":[OSD([subQ0]),TDD([makeQuery(id+"F0.imprint","IMPRINT",EDGE,{"disambiguationData":[TD([[makeQuery(id+"F0.imprint","INTERSECT",VERTEX,{"derivedFrom":[sQuery(id+"F0.wireOp",EDGE,"E18.3"),subQ0]}),-1.0]])],"derivedFrom":subQ0})])],"isStart":true});}
            var Q57;
            Q57=makeQuery(id+"F1.opExtrude","CAP_EDGE",EDGE,{"disambiguationData":[OSD([sQuery(id+"F0.wireOp",EDGE,"E19.1")])],"isStart":true});
            var Q58;
            {var subQ0=sQuery(id+"F0.wireOp",EDGE,"E1.4");Q58=makeQuery(id+"F1.opExtrude","CAP_EDGE",EDGE,{"disambiguationData":[OSD([subQ0]),TDD([makeQuery(id+"F0.imprint","IMPRINT",EDGE,{"disambiguationData":[TD([[makeQuery(id+"F0.imprint","INTERSECT",VERTEX,{"derivedFrom":[subQ0,sQuery(id+"F0.wireOp",EDGE,"E19.1")]}),-1.0]])],"derivedFrom":subQ0})])],"isStart":true});}
            var Q59;
            Q59=makeQuery(id+"F1.opExtrude","CAP_EDGE",EDGE,{"disambiguationData":[OSD([sQuery(id+"F0.wireOp",EDGE,"E19.5")])],"isStart":true});
            fillet(context, id + "F2", {"entities" : qUnion([Q0, Q1, Q2, Q3, Q4, Q5, Q6, Q7, Q8, Q9, Q10, Q11, Q12, Q13, Q14, Q15, Q16, Q17, Q18, Q19, Q20, Q21, Q22, Q23, Q24, Q25, Q26, Q27, Q28, Q29, Q30, Q31, Q32, Q33, Q34, Q35, Q36, Q37, Q38, Q39, Q40, Q41, Q42, Q43, Q44, Q45, Q46, Q47, Q48, Q49, Q50, Q51, Q52, Q53, Q54, Q55, Q56, Q57, Q58, Q59]), "radius" : 2.54 * mm, "tangentPropagation" : true, "allowEdgeOverflow" : false});
        }
        {
            var Q0;
            Q0=makeQuery(id+"F1.opExtrude","CAP_EDGE",EDGE,{"disambiguationData":[OSD([sQuery(id+"F0.wireOp",EDGE,"E3")])],"isStart":false});
            var Q1;
            Q1=makeQuery(id+"F1.opExtrude","CAP_EDGE",EDGE,{"disambiguationData":[OSD([sQuery(id+"F0.wireOp",EDGE,"E3")])],"isStart":true});
            var Q2;
            Q2=makeQuery(id+"F1.opExtrude","CAP_EDGE",EDGE,{"disambiguationData":[OSD([sQuery(id+"F0.wireOp",EDGE,"E12.3")])],"isStart":true});
            var Q3;
            Q3=makeQuery(id+"F1.opExtrude","CAP_EDGE",EDGE,{"disambiguationData":[OSD([sQuery(id+"F0.wireOp",EDGE,"E12.3")])],"isStart":false});
            var Q4;
            Q4=makeQuery(id+"F1.opExtrude","CAP_EDGE",EDGE,{"disambiguationData":[OSD([sQuery(id+"F0.wireOp",EDGE,"E12.2")])],"isStart":true});
            var Q5;
            Q5=makeQuery(id+"F1.opExtrude","CAP_EDGE",EDGE,{"disambiguationData":[OSD([sQuery(id+"F0.wireOp",EDGE,"E12.2")])],"isStart":false});
            var Q6;
            Q6=makeQuery(id+"F1.opExtrude","CAP_EDGE",EDGE,{"disambiguationData":[OSD([sQuery(id+"F0.wireOp",EDGE,"E12.1")])],"isStart":true});
            var Q7;
            {var subQ0=sQuery(id+"F0.wireOp",EDGE,"E1.4");Q7=makeQuery(id+"F1.opExtrude","CAP_EDGE",EDGE,{"disambiguationData":[OSD([subQ0]),TDD([makeQuery(id+"F0.imprint","IMPRINT",EDGE,{"disambiguationData":[TD([[makeQuery(id+"F0.imprint","INTERSECT",VERTEX,{"derivedFrom":[sQuery(id+"F0.wireOp",EDGE,"E1.3"),subQ0]}),-1.0]])],"derivedFrom":subQ0})])],"isStart":true});}
            var Q8;
            {var subQ0=sQuery(id+"F0.wireOp",EDGE,"E1.3");Q8=makeQuery(id+"F1.opExtrude","CAP_EDGE",EDGE,{"disambiguationData":[OSD([subQ0]),TDD([makeQuery(id+"F0.imprint","IMPRINT",EDGE,{"disambiguationData":[TD([[makeQuery(id+"F0.imprint","INTERSECT",VERTEX,{"derivedFrom":[subQ0,sQuery(id+"F0.wireOp",EDGE,"E12.4")]}),-1.0]])],"derivedFrom":subQ0})])],"isStart":true});}
            var Q9;
            Q9=makeQuery(id+"F1.opExtrude","CAP_EDGE",EDGE,{"disambiguationData":[OSD([sQuery(id+"F0.wireOp",EDGE,"E12.4")])],"isStart":true});
            var Q10;
            Q10=makeQuery(id+"F1.opExtrude","CAP_EDGE",EDGE,{"disambiguationData":[OSD([sQuery(id+"F0.wireOp",EDGE,"E13.1")])],"isStart":true});
            var Q11;
            Q11=makeQuery(id+"F1.opExtrude","CAP_EDGE",EDGE,{"disambiguationData":[OSD([sQuery(id+"F0.wireOp",EDGE,"E13.2")])],"isStart":true});
            var Q12;
            Q12=makeQuery(id+"F1.opExtrude","CAP_EDGE",EDGE,{"disambiguationData":[OSD([sQuery(id+"F0.wireOp",EDGE,"E13.3")])],"isStart":true});
            var Q13;
            Q13=makeQuery(id+"F1.opExtrude","CAP_EDGE",EDGE,{"disambiguationData":[OSD([sQuery(id+"F0.wireOp",EDGE,"E13.3")])],"isStart":false});
            var Q14;
            Q14=makeQuery(id+"F1.opExtrude","CAP_EDGE",EDGE,{"disambiguationData":[OSD([sQuery(id+"F0.wireOp",EDGE,"E13.4")])],"isStart":true});
            var Q15;
            Q15=makeQuery(id+"F1.opExtrude","CAP_EDGE",EDGE,{"disambiguationData":[OSD([sQuery(id+"F0.wireOp",EDGE,"E13.4")])],"isStart":false});
            var Q16;
            {var subQ0=sQuery(id+"F0.wireOp",EDGE,"E1.2");Q16=makeQuery(id+"F1.opExtrude","CAP_EDGE",EDGE,{"disambiguationData":[OSD([subQ0]),TDD([makeQuery(id+"F0.imprint","IMPRINT",EDGE,{"disambiguationData":[TD([[makeQuery(id+"F0.imprint","INTERSECT",VERTEX,{"derivedFrom":[subQ0,sQuery(id+"F0.wireOp",EDGE,"E13.4")]}),-1.0]])],"derivedFrom":subQ0})])],"isStart":false});}
            var Q17;
            {var subQ0=sQuery(id+"F0.wireOp",EDGE,"E1.2");Q17=makeQuery(id+"F1.opExtrude","CAP_EDGE",EDGE,{"disambiguationData":[OSD([subQ0]),TDD([makeQuery(id+"F0.imprint","IMPRINT",EDGE,{"disambiguationData":[TD([[makeQuery(id+"F0.imprint","INTERSECT",VERTEX,{"derivedFrom":[subQ0,sQuery(id+"F0.wireOp",EDGE,"E13.4")]}),-1.0]])],"derivedFrom":subQ0})])],"isStart":true});}
            var Q18;
            {var subQ0=sQuery(id+"F0.wireOp",EDGE,"E1.3");Q18=makeQuery(id+"F1.opExtrude","SWEPT_FACE",FACE,{"disambiguationData":[OSD([subQ0]),TDD([makeQuery(id+"F0.imprint","IMPRINT",EDGE,{"disambiguationData":[TD([[makeQuery(id+"F0.imprint","INTERSECT",VERTEX,{"derivedFrom":[subQ0,sQuery(id+"F0.wireOp",EDGE,"E13.1")]}),1.0]])],"derivedFrom":subQ0})])]});}
            var Q19;
            Q19=makeQuery(id+"F1.opExtrude","CAP_EDGE",EDGE,{"disambiguationData":[OSD([sQuery(id+"F0.wireOp",EDGE,"E12.1")])],"isStart":false});
            var Q20;
            {var subQ0=sQuery(id+"F0.wireOp",EDGE,"E1.4");Q20=makeQuery(id+"F1.opExtrude","CAP_EDGE",EDGE,{"disambiguationData":[OSD([subQ0]),TDD([makeQuery(id+"F0.imprint","IMPRINT",EDGE,{"disambiguationData":[TD([[makeQuery(id+"F0.imprint","INTERSECT",VERTEX,{"derivedFrom":[sQuery(id+"F0.wireOp",EDGE,"E1.3"),subQ0]}),-1.0]])],"derivedFrom":subQ0})])],"isStart":false});}
            var Q21;
            {var subQ0=sQuery(id+"F0.wireOp",EDGE,"E1.3");Q21=makeQuery(id+"F1.opExtrude","CAP_EDGE",EDGE,{"disambiguationData":[OSD([subQ0]),TDD([makeQuery(id+"F0.imprint","IMPRINT",EDGE,{"disambiguationData":[TD([[makeQuery(id+"F0.imprint","INTERSECT",VERTEX,{"derivedFrom":[subQ0,sQuery(id+"F0.wireOp",EDGE,"E12.4")]}),-1.0]])],"derivedFrom":subQ0})])],"isStart":false});}
            var Q22;
            Q22=makeQuery(id+"F1.opExtrude","CAP_EDGE",EDGE,{"disambiguationData":[OSD([sQuery(id+"F0.wireOp",EDGE,"E12.4")])],"isStart":false});
            var Q23;
            Q23=makeQuery(id+"F1.opExtrude","SWEPT_FACE",FACE,{"disambiguationData":[OSD([sQuery(id+"F0.wireOp",EDGE,"E11.2")])]});
            var Q24;
            Q24=makeQuery(id+"F1.opExtrude","SWEPT_FACE",FACE,{"disambiguationData":[OSD([sQuery(id+"F0.wireOp",EDGE,"E11.4")])]});
            var Q25;
            {var subQ0=sQuery(id+"F0.wireOp",EDGE,"E1.1");Q25=makeQuery(id+"F1.opExtrude","CAP_EDGE",EDGE,{"disambiguationData":[OSD([subQ0]),TDD([makeQuery(id+"F0.imprint","IMPRINT",EDGE,{"disambiguationData":[TD([[makeQuery(id+"F0.imprint","INTERSECT",VERTEX,{"derivedFrom":[subQ0,sQuery(id+"F0.wireOp",EDGE,"E11.5")]}),-1.0]])],"derivedFrom":subQ0})])],"isStart":true});}
            var Q26;
            {var subQ0=sQuery(id+"F0.wireOp",EDGE,"E1.1");Q26=makeQuery(id+"F1.opExtrude","CAP_EDGE",EDGE,{"disambiguationData":[OSD([subQ0]),TDD([makeQuery(id+"F0.imprint","IMPRINT",EDGE,{"disambiguationData":[TD([[makeQuery(id+"F0.imprint","INTERSECT",VERTEX,{"derivedFrom":[subQ0,sQuery(id+"F0.wireOp",EDGE,"E11.5")]}),-1.0]])],"derivedFrom":subQ0})])],"isStart":false});}
            var Q27;
            Q27=makeQuery(id+"F1.opExtrude","SWEPT_FACE",FACE,{"disambiguationData":[OSD([sQuery(id+"F0.wireOp",EDGE,"E14.2")])]});
            var Q28;
            {var subQ0=sQuery(id+"F0.wireOp",EDGE,"E1.0");Q28=makeQuery(id+"F1.opExtrude","SWEPT_FACE",FACE,{"disambiguationData":[OSD([subQ0]),TDD([makeQuery(id+"F0.imprint","IMPRINT",EDGE,{"disambiguationData":[TD([[makeQuery(id+"F0.imprint","INTERSECT",VERTEX,{"derivedFrom":[subQ0,sQuery(id+"F0.wireOp",EDGE,"E1.1")]}),1.0]])],"derivedFrom":subQ0})])]});}
            var Q29;
            Q29=makeQuery(id+"F1.opExtrude","SWEPT_FACE",FACE,{"disambiguationData":[OSD([sQuery(id+"F0.wireOp",EDGE,"E15.3")])]});
            var Q30;
            {var subQ0=sQuery(id+"F0.wireOp",EDGE,"E1.0");Q30=makeQuery(id+"F1.opExtrude","SWEPT_FACE",FACE,{"disambiguationData":[OSD([subQ0]),TDD([makeQuery(id+"F0.imprint","IMPRINT",EDGE,{"disambiguationData":[TD([[makeQuery(id+"F0.imprint","INTERSECT",VERTEX,{"derivedFrom":[subQ0,sQuery(id+"F0.wireOp",EDGE,"E1.5")]}),-1.0]])],"derivedFrom":subQ0})])]});}
            var Q31;
            Q31=makeQuery(id+"F1.opExtrude","SWEPT_FACE",FACE,{"disambiguationData":[OSD([sQuery(id+"F0.wireOp",EDGE,"E10.4")])]});
            var Q32;
            Q32=makeQuery(id+"F1.opExtrude","SWEPT_FACE",FACE,{"disambiguationData":[OSD([sQuery(id+"F0.wireOp",EDGE,"E10.1")])]});
            chamfer(context, id + "F3", {"entities" : qUnion([Q0, Q1, Q2, Q3, Q4, Q5, Q6, Q7, Q8, Q9, Q10, Q11, Q12, Q13, Q14, Q15, Q16, Q17, Q18, Q19, Q20, Q21, Q22, Q23, Q24, Q25, Q26, Q27, Q28, Q29, Q30, Q31, Q32]), "width" : 1.27 * mm, "tangentPropagation" : true});
        }
    });
